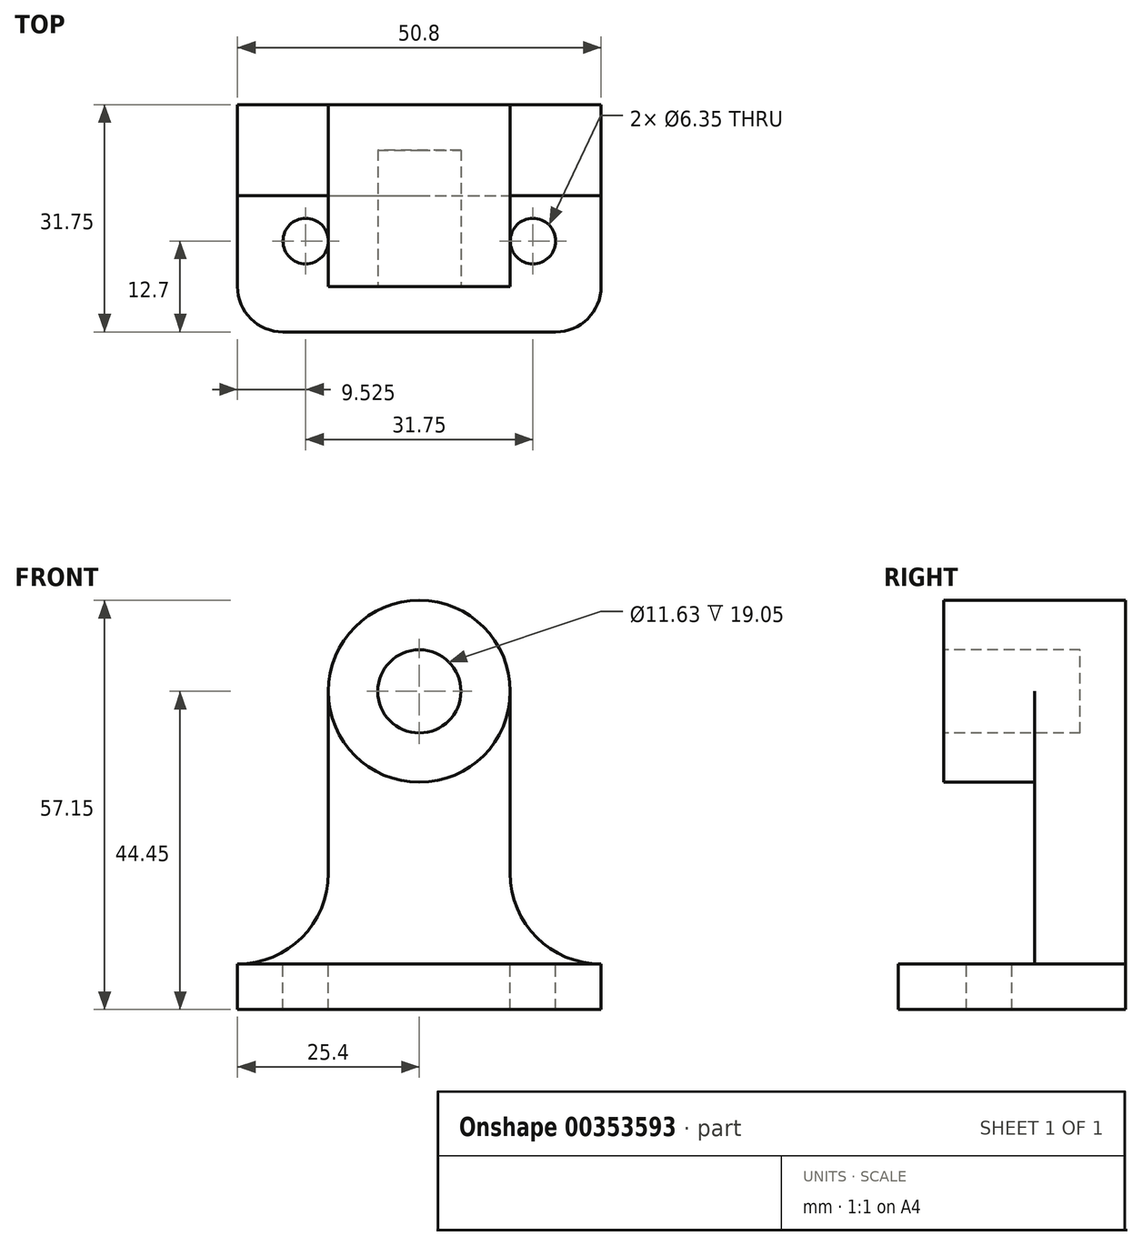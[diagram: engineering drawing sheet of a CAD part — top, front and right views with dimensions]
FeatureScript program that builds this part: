
annotation { "Feature Type Name" : "Feature", "Feature Type Description" : "" }
export const myFeature = defineFeature(function(context is Context, id is Id, definition is map)
    precondition{}
    {
        {
            var Q0;
            Q0=qCreatedBy(makeId("Top.planeOp"),FACE);
            var sketch = newSketch(context, id + "F0", { "sketchPlane" : qUnion([Q0])});
            skLineSegment(sketch, "E0.bottom", {"start": v(0, 0) * mm, "end": v(50.8, 0) * mm});
            skLineSegment(sketch, "E0.top", {"start": v(0, 31.75) * mm, "end": v(50.8, 31.75) * mm});
            skLineSegment(sketch, "E0.left", {"start": v(0, 0) * mm, "end": v(0, 31.75) * mm});
            skLineSegment(sketch, "E0.right", {"start": v(50.8, 0) * mm, "end": v(50.8, 31.75) * mm});
            skSolve(sketch);
        }
        {
            var Q0;
            Q0=makeQuery(id+"F0.imprint","IMPRINT",FACE,{"disambiguationData":[TD([[makeQuery(id+"F0.imprint","IMPRINT",EDGE,{"derivedFrom":sQuery(id+"F0.wireOp",EDGE,"E0.bottom")}),1.0]])]});
            extrude(context, id + "F1", {"entities" : qUnion([Q0]), "depth" : 6.35 * mm});
        }
        {
            var Q0;
            Q0=makeQuery(id+"F1.opExtrude","CAP_FACE",FACE,{"disambiguationData":[OSD([sQuery(id+"F0.wireOp",EDGE,"E0.bottom"),sQuery(id+"F0.wireOp",EDGE,"E0.top"),sQuery(id+"F0.wireOp",EDGE,"E0.left"),sQuery(id+"F0.wireOp",EDGE,"E0.right")])],"isStart":false});
            var sketch = newSketch(context, id + "F2", { "sketchPlane" : qUnion([Q0])});
            skLineSegment(sketch, "E1", {"start": v(0, 6.35) * mm, "end": v(0, 0) * mm});
            skLineSegment(sketch, "E2", {"start": v(0, 0) * mm, "end": v(6.35, 0) * mm});
            skLineSegment(sketch, "E3", {"start": v(50.8, 6.35) * mm, "end": v(50.8, 0) * mm});
            skLineSegment(sketch, "E4", {"start": v(50.8, 0) * mm, "end": v(44.45, 0) * mm});
            skArc(sketch, "E5", {"start": v(0, 6.35) * mm, "mid": v(1.86, 1.86) * mm, "end": v(6.35, 0) * mm});
            skArc(sketch, "E6", {"start": v(44.45, 0) * mm, "mid": v(48.94, 1.86) * mm, "end": v(50.8, 6.35) * mm});
            skSolve(sketch);
        }
        {
            var Q0;
            Q0=makeQuery(id+"F2.imprint","IMPRINT",FACE,{"disambiguationData":[TD([[makeQuery(id+"F2.imprint","IMPRINT",EDGE,{"derivedFrom":sQuery(id+"F2.wireOp",EDGE,"E1")}),-1.0]])]});
            var Q1;
            Q1=makeQuery(id+"F2.imprint","IMPRINT",FACE,{"disambiguationData":[TD([[makeQuery(id+"F2.imprint","IMPRINT",EDGE,{"derivedFrom":sQuery(id+"F2.wireOp",EDGE,"E3")}),1.0]])]});
            extrude(context, id + "F3", {"entities" : qUnion([Q0, Q1]), "operationType" : NewBodyOperationType.REMOVE, "oppositeDirection" : true, "depth" : 25.4 * mm});
        }
        {
            var Q0;
            Q0=makeQuery(id+"F1.opExtrude","CAP_FACE",FACE,{"disambiguationData":[OSD([sQuery(id+"F0.wireOp",EDGE,"E0.bottom"),sQuery(id+"F0.wireOp",EDGE,"E0.top"),sQuery(id+"F0.wireOp",EDGE,"E0.left"),sQuery(id+"F0.wireOp",EDGE,"E0.right")])],"isStart":false});
            var sketch = newSketch(context, id + "F4", { "sketchPlane" : qUnion([Q0])});
            skLineSegment(sketch, "E7.bottom", {"start": v(0, 31.75) * mm, "end": v(50.8, 31.75) * mm});
            skLineSegment(sketch, "E7.top", {"start": v(0, 19.05) * mm, "end": v(50.8, 19.05) * mm});
            skLineSegment(sketch, "E7.left", {"start": v(0, 31.75) * mm, "end": v(0, 19.05) * mm});
            skLineSegment(sketch, "E7.right", {"start": v(50.8, 31.75) * mm, "end": v(50.8, 19.05) * mm});
            skSolve(sketch);
        }
        {
            var Q0;
            Q0=makeQuery(id+"F4.imprint","IMPRINT",FACE,{"disambiguationData":[TD([[makeQuery(id+"F4.imprint","IMPRINT",EDGE,{"derivedFrom":sQuery(id+"F4.wireOp",EDGE,"E7.bottom")}),-1.0]])]});
            extrude(context, id + "F5", {"entities" : qUnion([Q0]), "operationType" : NewBodyOperationType.ADD, "depth" : 38.1 * mm});
        }
        {
            var Q0;
            Q0=makeQuery(id+"F1.opExtrude","CAP_FACE",FACE,{"disambiguationData":[OSD([sQuery(id+"F0.wireOp",EDGE,"E0.bottom"),sQuery(id+"F0.wireOp",EDGE,"E0.top"),sQuery(id+"F0.wireOp",EDGE,"E0.left"),sQuery(id+"F0.wireOp",EDGE,"E0.right")])],"isStart":false});
            var sketch = newSketch(context, id + "F6", { "sketchPlane" : qUnion([Q0])});
            skCircle(sketch, "E8", {"center": v(9.53, 12.7) * mm, "radius": 3.18 * mm});
            skPoint(sketch, "E8.centerSnap0", {"position": v(0, 12.7) * mm});
            skCircle(sketch, "E9", {"center": v(41.28, 12.7) * mm, "radius": 3.18 * mm});
            skSolve(sketch);
        }
        {
            var Q0;
            Q0 = qSketchRegion(id + "F6", true);
            extrude(context, id + "F7", {"entities" : qUnion([Q0]), "operationType" : NewBodyOperationType.REMOVE, "oppositeDirection" : true, "depth" : 25.4 * mm});
        }
        {
            var Q0;
            Q0=makeQuery(id+"F5.opExtrude","SWEPT_FACE",FACE,{"disambiguationData":[OSD([sQuery(id+"F4.wireOp",EDGE,"E7.top")])]});
            var sketch = newSketch(context, id + "F8", { "sketchPlane" : qUnion([Q0])});
            skLineSegment(sketch, "E10", {"start": v(12.7, 44.45) * mm, "end": v(12.7, 19.05) * mm});
            skLineSegment(sketch, "E11", {"start": v(38.1, 44.45) * mm, "end": v(38.1, 19.05) * mm});
            skArc(sketch, "E12", {"start": v(0, 6.35) * mm, "mid": v(8.98, 10.07) * mm, "end": v(12.7, 19.05) * mm});
            skArc(sketch, "E13", {"start": v(38.1, 19.05) * mm, "mid": v(41.82, 10.07) * mm, "end": v(50.8, 6.35) * mm});
            skArc(sketch, "E14", {"start": v(12.7, 44.45) * mm, "mid": v(25.4, 31.75) * mm, "end": v(38.1, 44.45) * mm});
            skSolve(sketch);
        }
        {
            var Q0;
            {var subQ0=sQuery(id+"F8.wireOp",EDGE,"E10");Q0=makeQuery(id+"F8.imprint","IMPRINT",FACE,{"disambiguationData":[TD([[makeQuery(id+"F8.imprint","IMPRINT",EDGE,{"derivedFrom":subQ0}),-1.0]])]});}
            var Q1;
            {var subQ0=sQuery(id+"F8.wireOp",EDGE,"E11");Q1=makeQuery(id+"F8.imprint","IMPRINT",FACE,{"disambiguationData":[TD([[makeQuery(id+"F8.imprint","IMPRINT",EDGE,{"derivedFrom":subQ0}),1.0]])]});}
            var Q2;
            {var subQ0=sQuery(id+"F8.wireOp",EDGE,"YEUsHBvE-bP2P-cDoy-vyaM-vCVGZaCbejHt");Q2=makeQuery(id+"F8.imprint","IMPRINT",FACE,{"disambiguationData":[TD([[makeQuery(id+"F8.imprint","IMPRINT",EDGE,{"derivedFrom":subQ0}),1.0]])]});}
            extrude(context, id + "F9", {"entities" : qUnion([Q0, Q1, Q2]), "operationType" : NewBodyOperationType.REMOVE, "oppositeDirection" : true, "depth" : 25.4 * mm});
        }
        {
            var Q0;
            {var subQ0=sQuery(id+"F8.wireOp",EDGE,"E10");Q0=makeQuery(id+"F8.imprint","IMPRINT",FACE,{"disambiguationData":[TD([[makeQuery(id+"F8.imprint","IMPRINT",EDGE,{"derivedFrom":subQ0}),-1.0]])]});}
            var Q1;
            {var subQ0=sQuery(id+"F8.wireOp",EDGE,"E14");Q1=makeQuery(id+"F8.imprint","IMPRINT",FACE,{"disambiguationData":[TD([[makeQuery(id+"F8.imprint","IMPRINT",EDGE,{"derivedFrom":subQ0}),1.0]])]});}
            var Q2;
            {var subQ0=sQuery(id+"F8.wireOp",EDGE,"E11");Q2=makeQuery(id+"F8.imprint","IMPRINT",FACE,{"disambiguationData":[TD([[makeQuery(id+"F8.imprint","IMPRINT",EDGE,{"derivedFrom":subQ0}),1.0]])]});}
            extrude(context, id + "F10", {"entities" : qUnion([Q0, Q1, Q2]), "operationType" : NewBodyOperationType.REMOVE, "oppositeDirection" : true, "depth" : 25.4 * mm});
        }
        {
            var Q0;
            Q0=makeQuery(id+"F5.opExtrude","SWEPT_FACE",FACE,{"disambiguationData":[OSD([sQuery(id+"F4.wireOp",EDGE,"E7.top")])]});
            var sketch = newSketch(context, id + "F11", { "sketchPlane" : qUnion([Q0])});
            skArc(sketch, "E15", {"start": v(38.1, 44.45) * mm, "mid": v(25.4, 57.15) * mm, "end": v(12.7, 44.45) * mm});
            skSolve(sketch);
        }
        {
            var Q0;
            Q0=makeQuery(id+"F11.imprint","IMPRINT",FACE,{"disambiguationData":[TD([[makeQuery(id+"F11.imprint","IMPRINT",EDGE,{"derivedFrom":sQuery(id+"F11.wireOp",EDGE,"E15")}),1.0]])]});
            extrude(context, id + "F12", {"entities" : qUnion([Q0]), "operationType" : NewBodyOperationType.ADD, "oppositeDirection" : true, "depth" : 12.7 * mm});
        }
        {
            var Q0;
            Q0=makeQuery(id+"F12.boolean.opBoolean","MERGE",FACE,{"derivedFrom":[makeQuery(id+"F5.opExtrude","SWEPT_FACE",FACE,{"disambiguationData":[OSD([sQuery(id+"F4.wireOp",EDGE,"E7.top")])]}),makeQuery(id+"F12.opExtrude","CAP_FACE",FACE,{"disambiguationData":[OSD([sQuery(id+"F8.wireOp",EDGE,"E14"),sQuery(id+"F11.wireOp",EDGE,"E15")])],"isStart":true})]});
            var sketch = newSketch(context, id + "F13", { "sketchPlane" : qUnion([Q0])});
            skArc(sketch, "E16", {"start": v(38.1, 44.45) * mm, "mid": v(25.4, 57.15) * mm, "end": v(12.7, 44.45) * mm});
            skArc(sketch, "E17", {"start": v(12.7, 44.45) * mm, "mid": v(25.4, 31.75) * mm, "end": v(38.1, 44.45) * mm});
            skSolve(sketch);
        }
        {
            var Q0;
            Q0=makeQuery(id+"F13.imprint","IMPRINT",FACE,{"disambiguationData":[TD([[makeQuery(id+"F13.imprint","IMPRINT",EDGE,{"derivedFrom":sQuery(id+"F13.wireOp",EDGE,"E16")}),1.0]])]});
            extrude(context, id + "F14", {"entities" : qUnion([Q0]), "operationType" : NewBodyOperationType.ADD, "depth" : 12.7 * mm});
        }
        {
            var Q0;
            Q0=makeQuery(id+"F14.opExtrude","CAP_FACE",FACE,{"disambiguationData":[OSD([sQuery(id+"F13.wireOp",EDGE,"E16"),sQuery(id+"F13.wireOp",EDGE,"E17")])],"isStart":false});
            var sketch = newSketch(context, id + "F15", { "sketchPlane" : qUnion([Q0])});
            skCircle(sketch, "E18", {"center": v(25.4, 44.45) * mm, "radius": 5.81 * mm});
            skSolve(sketch);
        }
        {
            var Q0;
            Q0=makeQuery(id+"F15.imprint","IMPRINT",FACE,{"disambiguationData":[TD([[makeQuery(id+"F15.imprint","IMPRINT",EDGE,{"derivedFrom":sQuery(id+"F15.wireOp",EDGE,"E18")}),1.0]])]});
            extrude(context, id + "F16", {"entities" : qUnion([Q0]), "operationType" : NewBodyOperationType.REMOVE, "oppositeDirection" : true, "depth" : 19.05 * mm});
        }
    });
